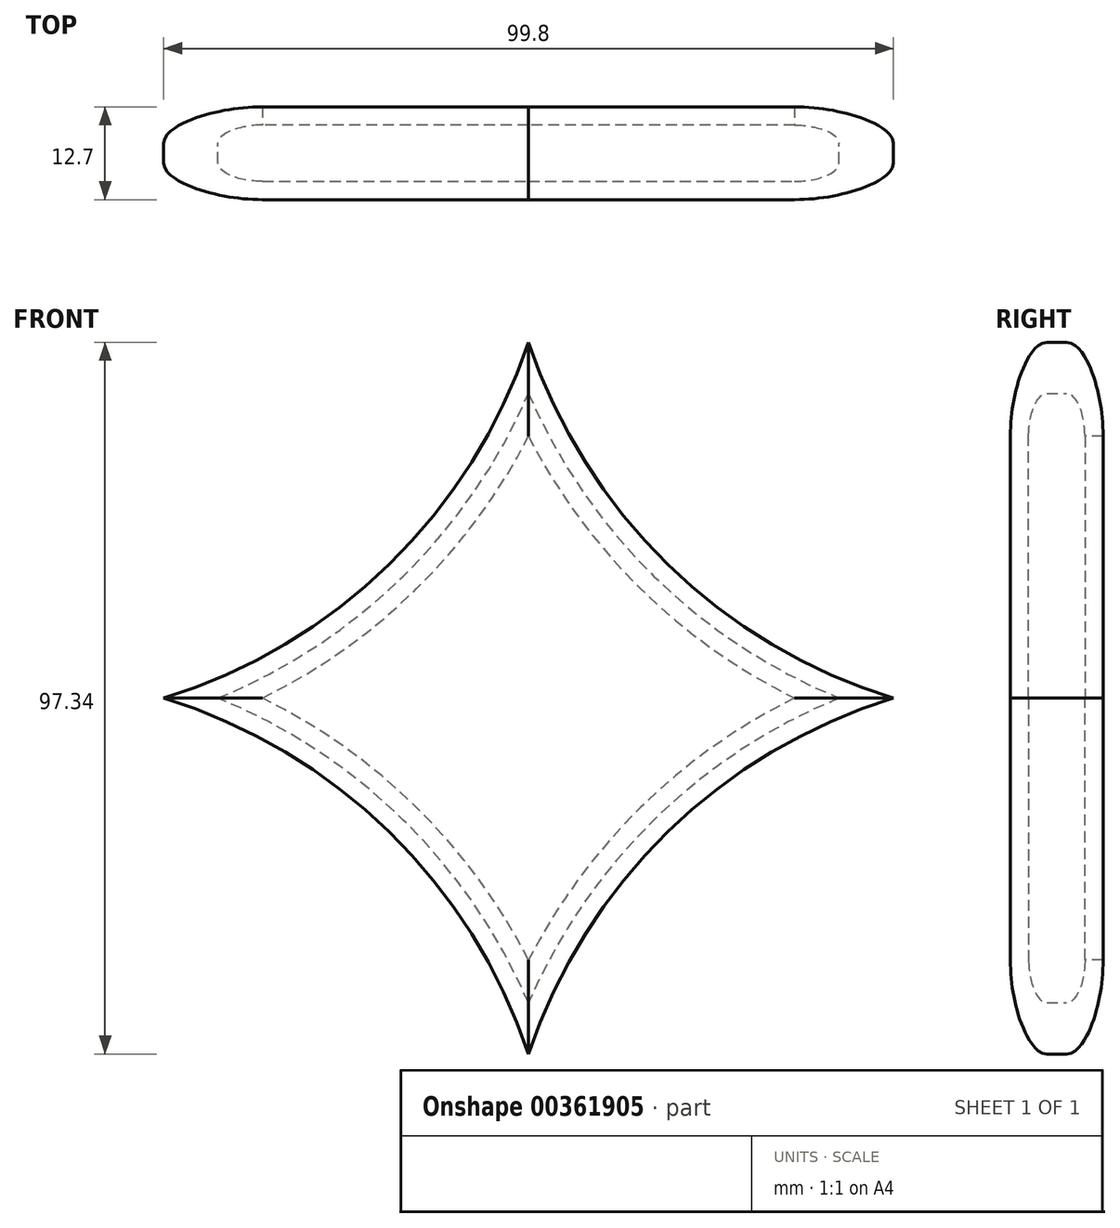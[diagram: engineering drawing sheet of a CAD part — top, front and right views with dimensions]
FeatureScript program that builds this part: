
annotation { "Feature Type Name" : "Feature", "Feature Type Description" : "" }
export const myFeature = defineFeature(function(context is Context, id is Id, definition is map)
    precondition{}
    {
        {
            var Q0;
            Q0=qCreatedBy(makeId("Front.planeOp"),FACE);
            var sketch = newSketch(context, id + "F0", { "sketchPlane" : qUnion([Q0])});
            skArc(sketch, "E0", {"start": v(0, -48.67) * mm, "mid": v(-19.06, -18.3) * mm, "end": v(-49.9, 0) * mm});
            skArc(sketch, "E1.MirrorCS", {"start": v(0, -48.67) * mm, "mid": v(19.06, -18.3) * mm, "end": v(49.9, 0) * mm});
            skArc(sketch, "E2.MirrorCS", {"start": v(0, 48.67) * mm, "mid": v(-19.06, 18.3) * mm, "end": v(-49.9, 0) * mm});
            skArc(sketch, "E3.MirrorCS", {"start": v(0, 48.67) * mm, "mid": v(19.06, 18.3) * mm, "end": v(49.9, 0) * mm});
            skSolve(sketch);
        }
        {
            var Q0;
            Q0 = qSketchRegion(id + "F0", true);
            extrude(context, id + "F1", {"entities" : qUnion([Q0]), "endBound" : BoundingType.SYMMETRIC, "depth" : 12.7 * mm});
        }
        {
            var Q0;
            Q0=makeQuery(id+"F1.opExtrude","CAP_EDGE",EDGE,{"disambiguationData":[OSD([sQuery(id+"F0.wireOp",EDGE,"E0")])],"isStart":true});
            var Q1;
            Q1=makeQuery(id+"F1.opExtrude","CAP_EDGE",EDGE,{"disambiguationData":[OSD([sQuery(id+"F0.wireOp",EDGE,"E1.MirrorCS")])],"isStart":true});
            var Q2;
            Q2=makeQuery(id+"F1.opExtrude","CAP_EDGE",EDGE,{"disambiguationData":[OSD([sQuery(id+"F0.wireOp",EDGE,"E2.MirrorCS")])],"isStart":true});
            var Q3;
            Q3=makeQuery(id+"F1.opExtrude","CAP_EDGE",EDGE,{"disambiguationData":[OSD([sQuery(id+"F0.wireOp",EDGE,"E3.MirrorCS")])],"isStart":true});
            fillet(context, id + "F2", {"entities" : qUnion([Q0, Q1, Q2, Q3]), "radius" : 5 * mm, "tangentPropagation" : true, "allowEdgeOverflow" : false});
        }
        {
            var Q0;
            Q0=makeQuery(id+"F1.opExtrude","CAP_EDGE",EDGE,{"disambiguationData":[OSD([sQuery(id+"F0.wireOp",EDGE,"E2.MirrorCS")])],"isStart":false});
            var Q1;
            Q1=makeQuery(id+"F1.opExtrude","CAP_EDGE",EDGE,{"disambiguationData":[OSD([sQuery(id+"F0.wireOp",EDGE,"E3.MirrorCS")])],"isStart":false});
            var Q2;
            Q2=makeQuery(id+"F1.opExtrude","CAP_EDGE",EDGE,{"disambiguationData":[OSD([sQuery(id+"F0.wireOp",EDGE,"E1.MirrorCS")])],"isStart":false});
            var Q3;
            Q3=makeQuery(id+"F1.opExtrude","CAP_EDGE",EDGE,{"disambiguationData":[OSD([sQuery(id+"F0.wireOp",EDGE,"E0")])],"isStart":false});
            fillet(context, id + "F3", {"entities" : qUnion([Q0, Q1, Q2, Q3]), "radius" : 5 * mm, "tangentPropagation" : true, "allowEdgeOverflow" : false});
        }
        {
            var Q0;
            Q0=makeQuery(id+"F1.opExtrude","CAP_FACE",FACE,{"disambiguationData":[OSD([sQuery(id+"F0.wireOp",EDGE,"E0"),sQuery(id+"F0.wireOp",EDGE,"E1.MirrorCS"),sQuery(id+"F0.wireOp",EDGE,"E2.MirrorCS"),sQuery(id+"F0.wireOp",EDGE,"E3.MirrorCS")])],"isStart":true});
            shell(context, id + "F4", {"entities" : qUnion([Q0]), "thickness" : 2.5 * mm});
        }
    });
